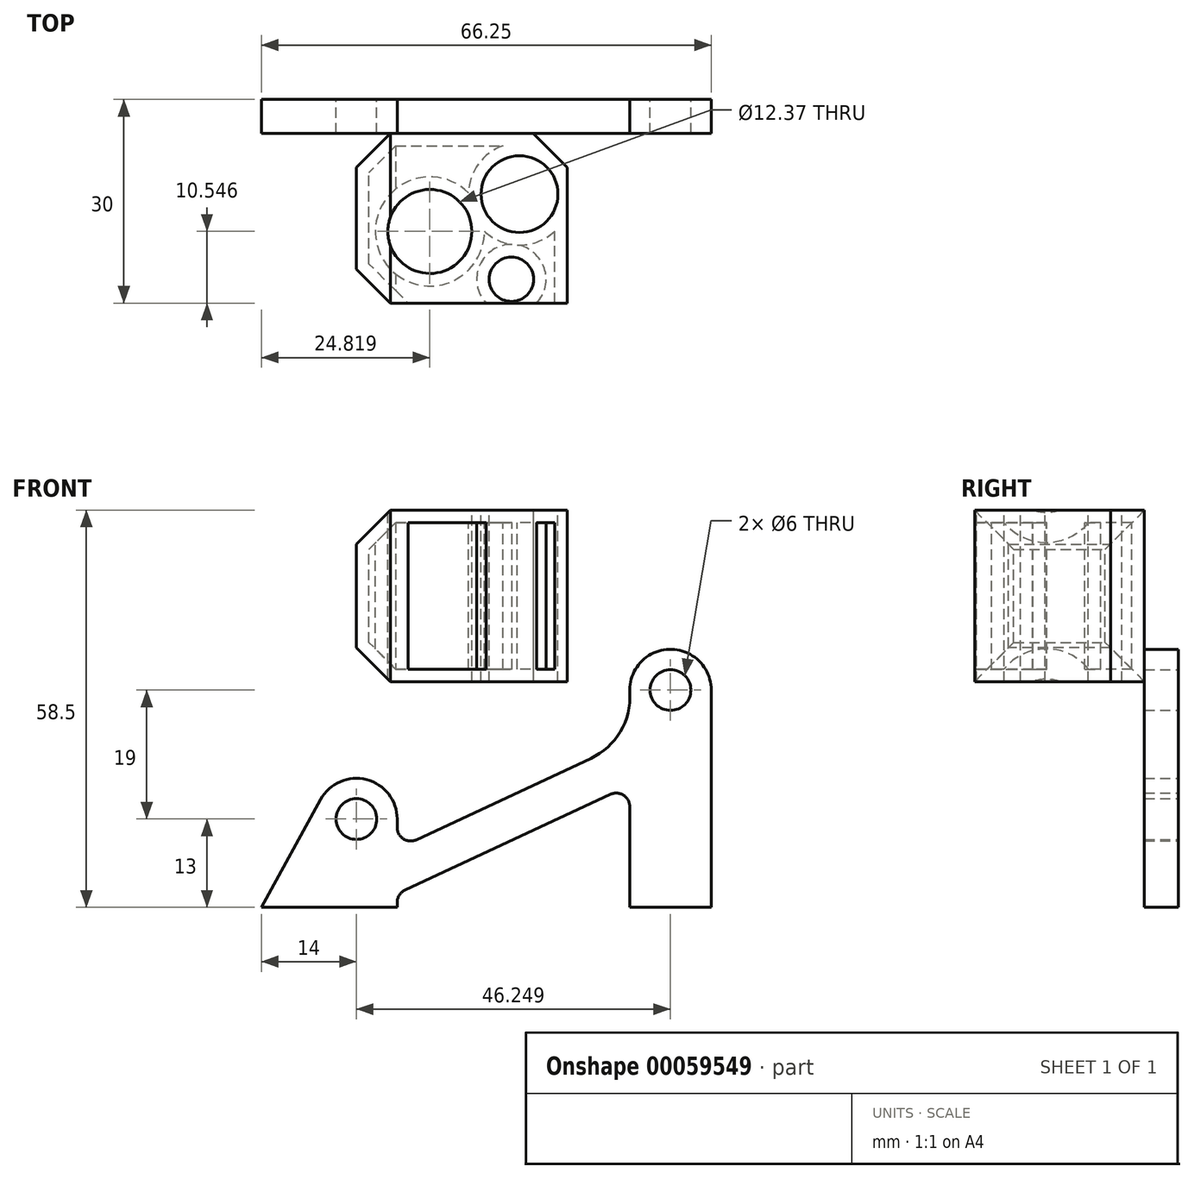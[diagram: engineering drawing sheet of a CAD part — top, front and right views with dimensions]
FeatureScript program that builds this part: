
annotation { "Feature Type Name" : "Feature", "Feature Type Description" : "" }
export const myFeature = defineFeature(function(context is Context, id is Id, definition is map)
    precondition{}
    {
        {
            var Q0;
            Q0=qCreatedBy(makeId("Front.planeOp"),FACE);
            var sketch = newSketch(context, id + "F0", { "sketchPlane" : qUnion([Q0])});
            skCircle(sketch, "E0", {"center": v(0, 0) * mm, "radius": 3 * mm});
            skCircle(sketch, "E1", {"center": v(46.25, 19) * mm, "radius": 3 * mm});
            skCircle(sketch, "E2", {"center": v(0, 0) * mm, "radius": 6 * mm});
            skCircle(sketch, "E3", {"center": v(46.25, 19) * mm, "radius": 6 * mm});
            skLineSegment(sketch, "E4", {"start": v(6, 0) * mm, "end": v(6, -1.24) * mm});
            skLineSegment(sketch, "E5", {"start": v(8.85, -3.05) * mm, "end": v(34.5, 8.91) * mm});
            skLineSegment(sketch, "E6", {"start": v(52.25, -13) * mm, "end": v(40.25, -13) * mm});
            skLineSegment(sketch, "E7", {"start": v(40.25, -13) * mm, "end": v(40.25, 1.83) * mm});
            skLineSegment(sketch, "E8", {"start": v(37.4, 3.64) * mm, "end": v(7.15, -10.46) * mm});
            skLineSegment(sketch, "E9", {"start": v(6, -12.27) * mm, "end": v(6, -13) * mm});
            skLineSegment(sketch, "E10", {"start": v(6, -13) * mm, "end": v(-14, -13) * mm});
            skLineSegment(sketch, "E11", {"start": v(-14, -13) * mm, "end": v(-5.26, 2.9) * mm});
            skPoint(sketch, "E12.visualSharp", {"position": v(6, -4.38) * mm});
            skArc(sketch, "E12.filletArc", {"start": v(6, -1.24) * mm, "mid": v(6.93, -2.93) * mm, "end": v(8.85, -3.05) * mm});
            skPoint(sketch, "E13.visualSharp", {"position": v(40.25, 4.97) * mm});
            skArc(sketch, "E13.filletArc", {"start": v(40.25, 1.83) * mm, "mid": v(39.32, 3.52) * mm, "end": v(37.4, 3.64) * mm});
            skPoint(sketch, "E14.visualSharp", {"position": v(6, -11) * mm});
            skArc(sketch, "E14.filletArc", {"start": v(7.15, -10.46) * mm, "mid": v(6.31, -11.2) * mm, "end": v(6, -12.27) * mm});
            skLineSegment(sketch, "E15", {"start": v(52.25, -13) * mm, "end": v(52.25, 19) * mm});
            skArc(sketch, "E16", {"start": v(34.5, 8.91) * mm, "mid": v(38.88, 12.88) * mm, "end": v(40.26, 18.62) * mm});
            skSolve(sketch);
        }
        {
            var Q0;
            Q0=makeQuery(id+"F0.imprint","IMPRINT",FACE,{"disambiguationData":[TD([[makeQuery(id+"F0.imprint","IMPRINT",EDGE,{"derivedFrom":sQuery(id+"F0.wireOp",EDGE,"E0")}),-1.0]])]});
            var Q1;
            {var subQ2=sQuery(id+"F0.wireOp",EDGE,"E4");Q1=makeQuery(id+"F0.imprint","IMPRINT",FACE,{"disambiguationData":[TD([[makeQuery(id+"F0.imprint","IMPRINT",EDGE,{"derivedFrom":subQ2}),-1.0]])]});}
            var Q2;
            Q2=makeQuery(id+"F0.imprint","IMPRINT",FACE,{"disambiguationData":[TD([[makeQuery(id+"F0.imprint","IMPRINT",EDGE,{"derivedFrom":sQuery(id+"F0.wireOp",EDGE,"E1")}),-1.0]])]});
            extrude(context, id + "F1", {"entities" : qUnion([Q0, Q1, Q2]), "depth" : 5 * mm});
        }
        {
            var Q0;
            Q0=makeQuery(id+"F1.opExtrude","CAP_FACE",FACE,{"disambiguationData":[OSD([sQuery(id+"F0.wireOp",EDGE,"E0"),sQuery(id+"F0.wireOp",EDGE,"E1"),sQuery(id+"F0.wireOp",EDGE,"E2"),sQuery(id+"F0.wireOp",EDGE,"E3"),sQuery(id+"F0.wireOp",EDGE,"E4"),sQuery(id+"F0.wireOp",EDGE,"E5"),sQuery(id+"F0.wireOp",EDGE,"E6"),sQuery(id+"F0.wireOp",EDGE,"E7"),sQuery(id+"F0.wireOp",EDGE,"E8"),sQuery(id+"F0.wireOp",EDGE,"E9"),sQuery(id+"F0.wireOp",EDGE,"E10"),sQuery(id+"F0.wireOp",EDGE,"E11"),sQuery(id+"F0.wireOp",EDGE,"E12.filletArc"),sQuery(id+"F0.wireOp",EDGE,"E13.filletArc"),sQuery(id+"F0.wireOp",EDGE,"E14.filletArc"),sQuery(id+"F0.wireOp",EDGE,"E15"),sQuery(id+"F0.wireOp",EDGE,"E16")])],"isStart":false});
            var sketch = newSketch(context, id + "F2", { "sketchPlane" : qUnion([Q0])});
            skLineSegment(sketch, "E17.bottom", {"start": v(0, 45.5) * mm, "end": v(31.02, 45.5) * mm});
            skLineSegment(sketch, "E17.top", {"start": v(0, 20.23) * mm, "end": v(31.02, 20.23) * mm});
            skLineSegment(sketch, "E17.left", {"start": v(0, 45.5) * mm, "end": v(0, 20.23) * mm});
            skLineSegment(sketch, "E17.right", {"start": v(31.02, 45.5) * mm, "end": v(31.02, 20.23) * mm});
            skSolve(sketch);
        }
        {
            var Q0;
            Q0=makeQuery(id+"F2.imprint","IMPRINT",FACE,{"disambiguationData":[TD([[makeQuery(id+"F2.imprint","IMPRINT",EDGE,{"derivedFrom":sQuery(id+"F2.wireOp",EDGE,"E17.bottom")}),-1.0]])]});
            extrude(context, id + "F7", {"entities" : qUnion([Q0]), "depth" : 25 * mm});
        }
        {
            var Q0;
            Q0=makeQuery(id+"F7.opExtrude","SWEPT_FACE",FACE,{"disambiguationData":[OSD([sQuery(id+"F2.wireOp",EDGE,"E17.bottom")])]});
            var sketch = newSketch(context, id + "F3", { "sketchPlane" : qUnion([Q0])});
            skCircle(sketch, "E18", {"center": v(24.02, -13.95) * mm, "radius": 5.66 * mm});
            skCircle(sketch, "E19", {"center": v(10.82, -19.45) * mm, "radius": 6.19 * mm});
            skCircle(sketch, "E20", {"center": v(22.82, -26.5) * mm, "radius": 3.26 * mm});
            skSolve(sketch);
        }
        {
            var Q0;
            Q0=makeQuery(id+"F3.imprint","IMPRINT",FACE,{"disambiguationData":[TD([[makeQuery(id+"F3.imprint","IMPRINT",EDGE,{"derivedFrom":sQuery(id+"F3.wireOp",EDGE,"E19")}),1.0]])]});
            var Q1;
            Q1=makeQuery(id+"F3.imprint","IMPRINT",FACE,{"disambiguationData":[TD([[makeQuery(id+"F3.imprint","IMPRINT",EDGE,{"derivedFrom":sQuery(id+"F3.wireOp",EDGE,"E18")}),1.0]])]});
            var Q2;
            Q2=makeQuery(id+"F3.imprint","IMPRINT",FACE,{"disambiguationData":[TD([[makeQuery(id+"F3.imprint","IMPRINT",EDGE,{"derivedFrom":sQuery(id+"F3.wireOp",EDGE,"E20")}),1.0]])]});
            extrude(context, id + "F4", {"entities" : qUnion([Q0, Q1, Q2]), "operationType" : NewBodyOperationType.REMOVE, "endBound" : BoundingType.THROUGH_ALL, "oppositeDirection" : true, "depth" : 25 * mm});
        }
        {
            var Q0;
            Q0=makeQuery(id+"F7.opExtrude","CAP_EDGE",EDGE,{"disambiguationData":[OSD([sQuery(id+"F2.wireOp",EDGE,"E17.left")])],"isStart":true});
            var Q1;
            Q1=makeQuery(id+"F7.opExtrude","SWEPT_EDGE",EDGE,{"disambiguationData":[OSD([sQuery(id+"F2.wireOp",EDGE,"E17.bottom"),sQuery(id+"F2.wireOp",EDGE,"E17.left")])]});
            var Q2;
            Q2=makeQuery(id+"F7.opExtrude","CAP_EDGE",EDGE,{"disambiguationData":[OSD([sQuery(id+"F2.wireOp",EDGE,"E17.left")])],"isStart":false});
            var Q3;
            Q3=makeQuery(id+"F7.opExtrude","SWEPT_EDGE",EDGE,{"disambiguationData":[OSD([sQuery(id+"F2.wireOp",EDGE,"E17.top"),sQuery(id+"F2.wireOp",EDGE,"E17.left")])]});
            var Q4;
            Q4=makeQuery(id+"F7.opExtrude","SWEPT_EDGE",EDGE,{"disambiguationData":[OSD([sQuery(id+"F2.wireOp",EDGE,"E17.top"),sQuery(id+"F2.wireOp",EDGE,"E17.left")])]});
            var Q5;
            Q5=makeQuery(id+"F7.opExtrude","CAP_EDGE",EDGE,{"disambiguationData":[OSD([sQuery(id+"F2.wireOp",EDGE,"E17.right")])],"isStart":true});
            chamfer(context, id + "F5", {"entities" : qUnion([Q0, Q1, Q2, Q3, Q4, Q5]), "width" : 5 * mm, "tangentPropagation" : true});
        }
        {
            var Q0;
            Q0=makeQuery(id+"F7.opExtrude","CAP_FACE",FACE,{"disambiguationData":[OSD([sQuery(id+"F2.wireOp",EDGE,"E17.bottom"),sQuery(id+"F2.wireOp",EDGE,"E17.top"),sQuery(id+"F2.wireOp",EDGE,"E17.left"),sQuery(id+"F2.wireOp",EDGE,"E17.right")])],"isStart":false});
            shell(context, id + "F6", {"entities" : qUnion([Q0]), "thickness" : 1.85 * mm});
        }
    });
